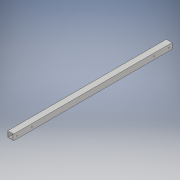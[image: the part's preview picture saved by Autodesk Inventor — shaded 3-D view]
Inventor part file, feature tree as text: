
AUTODESK INVENTOR PART (.ipt)
format: ipt  version: 2018 (Build 220112000, 112)  size: 118,272 bytes
history: native  units: in
note: dims shown in document units (in); Inventor stores cm internally (conversion verified against a paired STEP export)
features: extrude x2, sketch x2
ambient origin geometry x8: Origin, YZ Plane, XZ Plane, XY Plane, X Axis, Y Axis, Z Axis, Center Point
bodies: Solid1 (feature_tree)
feature tree (4):
  extrude  "Extrusion1"  Depth=1.0in
  extrude  "Extrusion3"  Depth=27.362in TaperAngle=0.0deg
  sketch  "Sketch1"  dims[d0=1.0in d1=1.0in]
  sketch  "Sketch2"  dims[d2=0.125in d3=27.362in d4=0.0in d5=0.5in d7=0.5in d8=0.197in d11=2.632in d12=2.632in d13=27.362in d14=0.0in]
